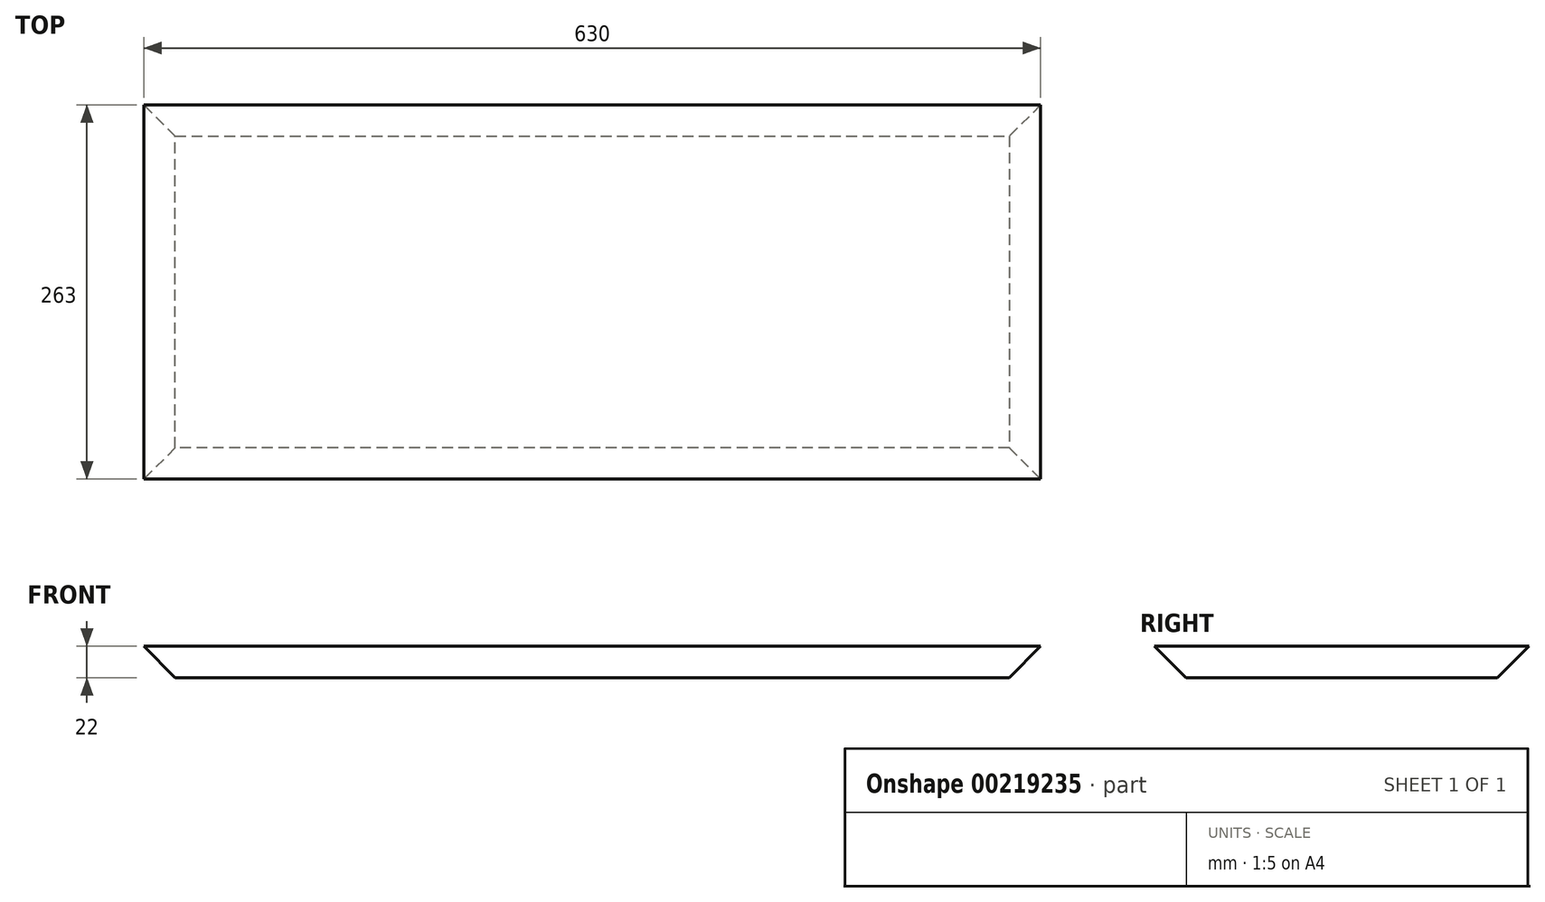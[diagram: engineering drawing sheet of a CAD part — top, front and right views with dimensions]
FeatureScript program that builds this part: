
annotation { "Feature Type Name" : "Feature", "Feature Type Description" : "" }
export const myFeature = defineFeature(function(context is Context, id is Id, definition is map)
    precondition{}
    {
        {
            var Q0;
            Q0=qCreatedBy(makeId("Top.planeOp"),FACE);
            var sketch = newSketch(context, id + "F0", { "sketchPlane" : qUnion([Q0])});
            skLineSegment(sketch, "E0.bottom", {"start": v(315, 131.5) * mm, "end": v(-315, 131.5) * mm});
            skLineSegment(sketch, "E0.top", {"start": v(315, -131.5) * mm, "end": v(-315, -131.5) * mm});
            skLineSegment(sketch, "E0.left", {"start": v(315, 131.5) * mm, "end": v(315, -131.5) * mm});
            skLineSegment(sketch, "E0.right", {"start": v(-315, 131.5) * mm, "end": v(-315, -131.5) * mm});
            skPoint(sketch, "E0.middle", {"position": v(0, 0) * mm});
            skSolve(sketch);
        }
        {
            var Q0;
            Q0 = qSketchRegion(id + "F0", true);
            var Q1;
            Q1=makeQuery(id+"F0.imprint","IMPRINT",FACE,{"disambiguationData":[TD([[makeQuery(id+"F0.imprint","IMPRINT",EDGE,{"derivedFrom":sQuery(id+"F0.wireOp",EDGE,"E0.bottom")}),1.0]])]});
            extrude(context, id + "F1", {"entities" : qUnion([Q0, Q1]), "depth" : 22 * mm});
        }
        {
            var Q0;
            Q0=makeQuery(id+"F1.opExtrude","CAP_EDGE",EDGE,{"disambiguationData":[OSD([sQuery(id+"F0.wireOp",EDGE,"E0.bottom")])],"isStart":true});
            var Q1;
            Q1=makeQuery(id+"F1.opExtrude","CAP_EDGE",EDGE,{"disambiguationData":[OSD([sQuery(id+"F0.wireOp",EDGE,"E0.left")])],"isStart":true});
            var Q2;
            Q2=makeQuery(id+"F1.opExtrude","CAP_EDGE",EDGE,{"disambiguationData":[OSD([sQuery(id+"F0.wireOp",EDGE,"E0.top")])],"isStart":true});
            var Q3;
            Q3=makeQuery(id+"F1.opExtrude","CAP_FACE",FACE,{"disambiguationData":[OSD([sQuery(id+"F0.wireOp",EDGE,"E0.bottom"),sQuery(id+"F0.wireOp",EDGE,"E0.top"),sQuery(id+"F0.wireOp",EDGE,"E0.left"),sQuery(id+"F0.wireOp",EDGE,"E0.right")])],"isStart":true});
            chamfer(context, id + "F2", {"entities" : qUnion([Q0, Q1, Q2, Q3]), "width" : 22 * mm, "tangentPropagation" : true});
        }
    });
